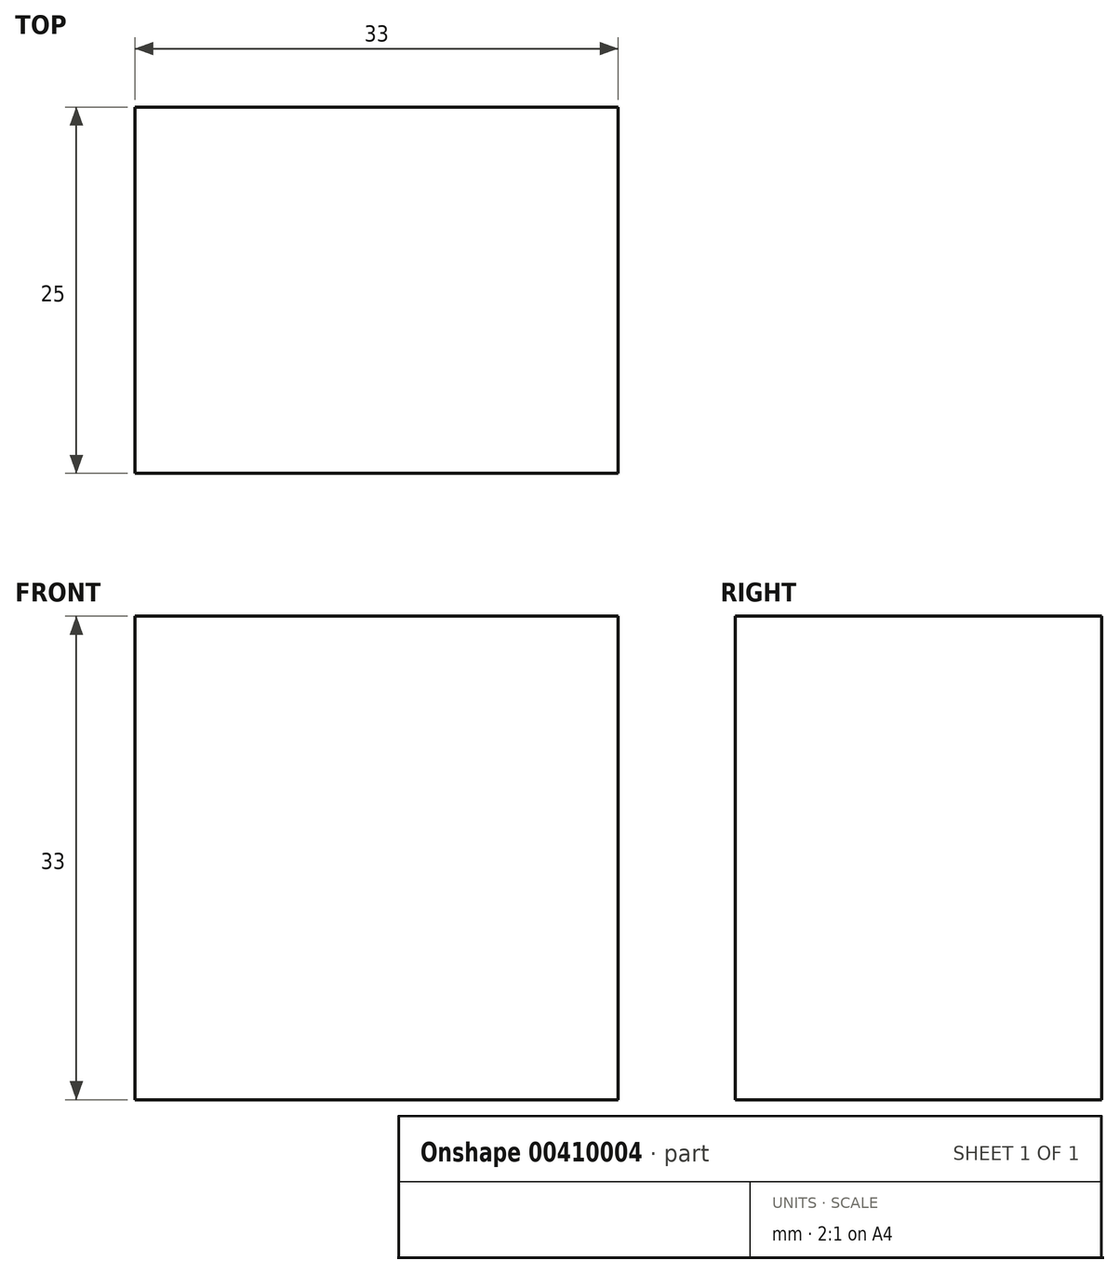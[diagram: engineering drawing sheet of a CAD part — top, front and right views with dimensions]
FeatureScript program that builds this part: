
annotation { "Feature Type Name" : "Feature", "Feature Type Description" : "" }
export const myFeature = defineFeature(function(context is Context, id is Id, definition is map)
    precondition{}
    {
        {
            var Q0;
            Q0=qCreatedBy(makeId("Front.planeOp"),FACE);
            var sketch = newSketch(context, id + "F0", { "sketchPlane" : qUnion([Q0])});
            skLineSegment(sketch, "E0.bottom", {"start": v(16.5, -16.5) * mm, "end": v(-16.5, -16.5) * mm});
            skLineSegment(sketch, "E0.top", {"start": v(16.5, 16.5) * mm, "end": v(-16.5, 16.5) * mm});
            skLineSegment(sketch, "E0.left", {"start": v(16.5, -16.5) * mm, "end": v(16.5, 16.5) * mm});
            skLineSegment(sketch, "E0.right", {"start": v(-16.5, -16.5) * mm, "end": v(-16.5, 16.5) * mm});
            skPoint(sketch, "E0.middle", {"position": v(0, 0) * mm});
            skSolve(sketch);
        }
        {
            var Q0;
            Q0 = qSketchRegion(id + "F0", true);
            extrude(context, id + "F1", {"entities" : qUnion([Q0]), "depth" : 25 * mm});
        }
    });
